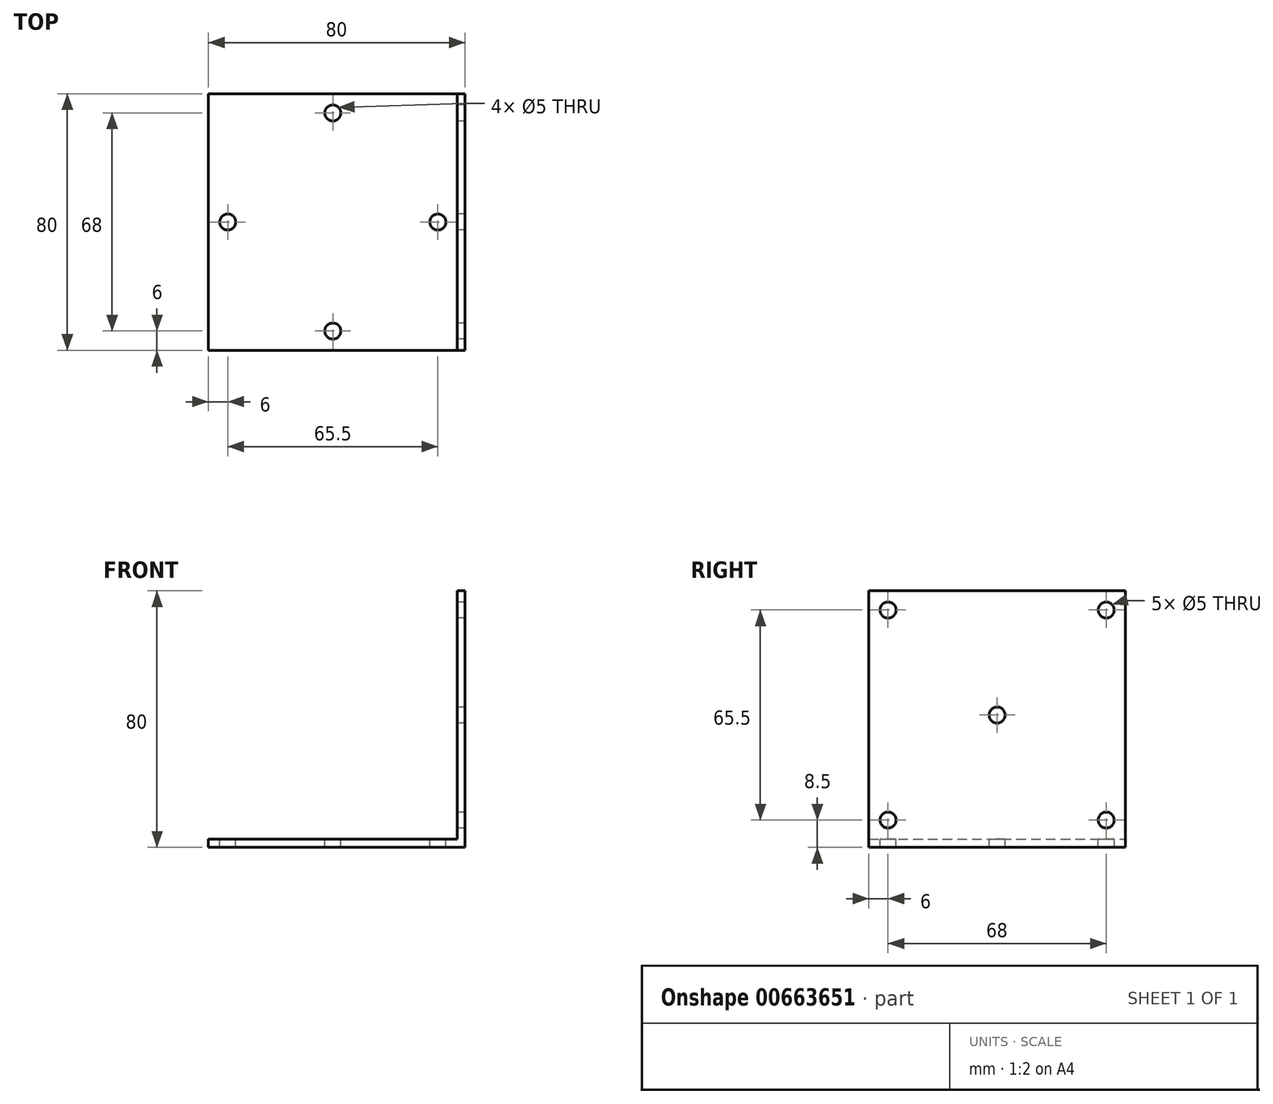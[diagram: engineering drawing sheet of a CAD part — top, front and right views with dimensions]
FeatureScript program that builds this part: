
annotation { "Feature Type Name" : "Feature", "Feature Type Description" : "" }
export const myFeature = defineFeature(function(context is Context, id is Id, definition is map)
    precondition{}
    {
        {
            var Q0;
            Q0=qCreatedBy(makeId("Front.planeOp"),FACE);
            var sketch = newSketch(context, id + "F0", { "sketchPlane" : qUnion([Q0])});
            skLineSegment(sketch, "E0", {"start": v(-80, 0) * mm, "end": v(0, 0) * mm});
            skLineSegment(sketch, "E1", {"start": v(0, 0) * mm, "end": v(0, 80) * mm});
            skLineSegment(sketch, "E2.0", {"start": v(-2.5, 2.5) * mm, "end": v(-2.5, 80) * mm});
            skLineSegment(sketch, "E2.1", {"start": v(-80, 2.5) * mm, "end": v(-2.5, 2.5) * mm});
            skLineSegment(sketch, "E3", {"start": v(-80, 2.5) * mm, "end": v(-80, 0) * mm});
            skLineSegment(sketch, "E4", {"start": v(-2.5, 80) * mm, "end": v(0, 80) * mm});
            skSolve(sketch);
        }
        {
            var Q0;
            Q0=qSketchRegion(id+"F0",true);
            extrude(context, id + "F1", {"entities" : qUnion([Q0]), "depth" : 80 * mm, "offsetDistance" : 25 * mm, "symmetric" : true});
        }
        {
            var Q0;
            Q0=makeQuery(id+"F1.opExtrude","SWEPT_FACE",FACE,{"disambiguationData":[OSD([sQuery(id+"F0.wireOp",EDGE,"E2.0")])]});
            var sketch = newSketch(context, id + "F2", { "sketchPlane" : qUnion([Q0])});
            skLineSegment(sketch, "E5", {"start": v(0, 80) * mm, "end": v(0, 2.5) * mm, "construction": true});
            skCircle(sketch, "E6", {"center": v(0, 41.25) * mm, "radius": 2.5 * mm});
            skCircle(sketch, "E7", {"center": v(-34, 8.5) * mm, "radius": 2.5 * mm});
            skCircle(sketch, "E8", {"center": v(-34, 74) * mm, "radius": 2.5 * mm});
            skCircle(sketch, "E9.MirrorC", {"center": v(34, 74) * mm, "radius": 2.5 * mm});
            skCircle(sketch, "E10.MirrorC", {"center": v(34, 8.5) * mm, "radius": 2.5 * mm});
            skSolve(sketch);
        }
        {
            var Q0;
            Q0=qSketchRegion(id+"F2",true);
            extrude(context, id + "F3", {"entities" : qUnion([Q0]), "operationType" : NewBodyOperationType.REMOVE, "oppositeDirection" : true, "depth" : 25 * mm, "offsetDistance" : 25 * mm});
        }
        {
            var Q0;
            Q0=makeQuery(id+"F1.opExtrude","SWEPT_FACE",FACE,{"disambiguationData":[OSD([sQuery(id+"F0.wireOp",EDGE,"E2.1")])]});
            var sketch = newSketch(context, id + "F4", { "sketchPlane" : qUnion([Q0])});
            skLineSegment(sketch, "E11", {"start": v(-80, 0) * mm, "end": v(-2.5, 0) * mm, "construction": true});
            skLineSegment(sketch, "E12", {"start": v(-41.25, 40) * mm, "end": v(-41.25, -40) * mm, "construction": true});
            skCircle(sketch, "E13", {"center": v(-74, 0) * mm, "radius": 2.5 * mm});
            skCircle(sketch, "E14", {"center": v(-41.25, 34) * mm, "radius": 2.5 * mm});
            skCircle(sketch, "E15.MirrorC", {"center": v(-41.25, -34) * mm, "radius": 2.5 * mm});
            skCircle(sketch, "E16.MirrorC", {"center": v(-8.5, 0) * mm, "radius": 2.5 * mm});
            skSolve(sketch);
        }
        {
            var Q0;
            Q0=qSketchRegion(id+"F4",true);
            extrude(context, id + "F5", {"entities" : qUnion([Q0]), "operationType" : NewBodyOperationType.REMOVE, "oppositeDirection" : true, "depth" : 25 * mm, "offsetDistance" : 25 * mm});
        }
    });
